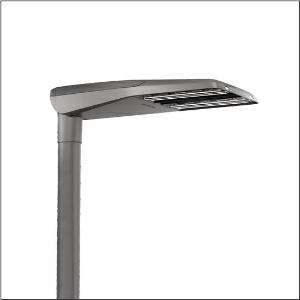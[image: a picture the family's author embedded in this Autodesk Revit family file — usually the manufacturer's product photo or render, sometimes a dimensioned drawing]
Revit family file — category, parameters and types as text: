
# Revit family: streetlight_sl_11_iq_midi___st1_0ab_5xc3n41f08me_2825
name_source: partatom
category: Lighting Fixtures
units: mm (PartAtom-declared; Revit-internal decimal feet)

## family parameters
Cut with Voids When Loaded = No
Host = Face
Light Source = No
Part Type = Normal
Room Calculation Point = No
Round Connector Dimension = Use Diameter
Shared = No

## types (1)
- --- (1 x LED, 15930 lm, 124.7 W, 4000K)
    Apparent Load = 125 VA
    CIE Flux Codes = 29 63 95 100 100
    Color Rendering = 70
    Color Temperature = 4000K
    Default Elevation = 1800 mm
    Description = Streetlight SL 11 iQ midi, mast luminaire, primary light control with 3 zone facetted reflector, of plastic, silver coated, highly specular, primary optical cover: cover, of PMMA, transparent, light distribution: ST1.0aB, light emission: direct distribution, primary light characteristic: asymmetric, installation type: post-top, side-entry, LED, High Power LED, rated luminous flux: 15.930lm, luminous efficacy: 128lm/W, light colour: 740, colour temperature: 4000K, control: optimised constant luminous flux control (CLO 2.0), Street-Remote, Desk-Remote (wireless, voltage-free reading and setting of iQ features in the workshop via application-optimized NFC function/RFID function), Light-Fading, Smart-Wire, Night-Set, Lumen-Switch, Temp-Guard, Auto-Match, with cable H07RN-F 5x 1.5mm², mains connection: 230..240V, AC, 50/60Hz, connection cable pre-assembled, cable length: 12,5m, start of lifetime: 125W, end of service life: 132W, reduction: 57W, luminaire housing, of diecast aluminium, powder-coated, Siteco® metallic grey (DB 702S), please order mast flange separately, inclination adjustable without tools: 0°, 5°, 10°, 15° (post-top) | 0°, -5°, -10°, -15° (side-entry), sealing non-destructively replaceable, multi-level sealing system, length: 780mm, width: 376mm, height: 118mm, mast flange for spigot size: 42mm (side-entry): 5XC10008XM4, 60/48mm (side-entry/post-top): 5XC10108XM2, 76/60mm (side-entry/post-top): 5XC10108XM1, equipment: Power, protection rating (complete): IP66, insulation class (complete): insulation class II (safety insulation), certification: CE, ENEC, VDE, impact resistance: IK09, permissible operating ambient temperature for outdoor applications: -25..+50°C, standard-compliant lighting for roads and squares, Environmental Product Declaration (EPD) tested and certified by an independent institute, packaging unit: 1 piece

Light Distribution: ST1.0aB
    Height = 118 mm
    Lamp = 1 x LED
    Lamp Light Flux = 15930 lm
    Lamp Power = 124.7 W
    Lamp count = 1
    Length = 780 mm
    Luminous efficacy = 128 lm/W
    Manufacturer = Siteco
    ModVariant = No
    Model = 5XC3N41F08ME
    Number of Poles = 1
    OnlyDefault = Yes
    Power Factor = 1
    Product Name = Streetlight SL 11 iQ midi | ST1.0aB
    Product group = mast luminaire | pylon top
    ProductGroupID = 6100
    Protection Class = Protection class II
    Protection Degree = IP 66
    RLX_Detail_Level = 1
    RLX_Emergency_Light_Flux = 0 lm
    RLX_Emergency_Type = 0
    RLX_Emergency_Type_DB = No
    RlxData = <blob elided: 70217 chars, md5=37d1ef4e>
    Socket = socket
    Standby Power = 0 W
    System Light Flux = 15930 lm
    System Power = 125 W
    Type Comments = factory setting: luminous flux: 100 % | dim-lin: 254 | 557 mA
    Type Image = l_1005960.jpg
    URL = http://relux.com
    VarID = @adj_020221
    Voltage = 0 V
    Weight = 0.00 kg
    Width = 376 mm

## geometry (parser evidence)
native form markers: Blend x4, Sweep x11
no freeform markers — native parametric forms only
